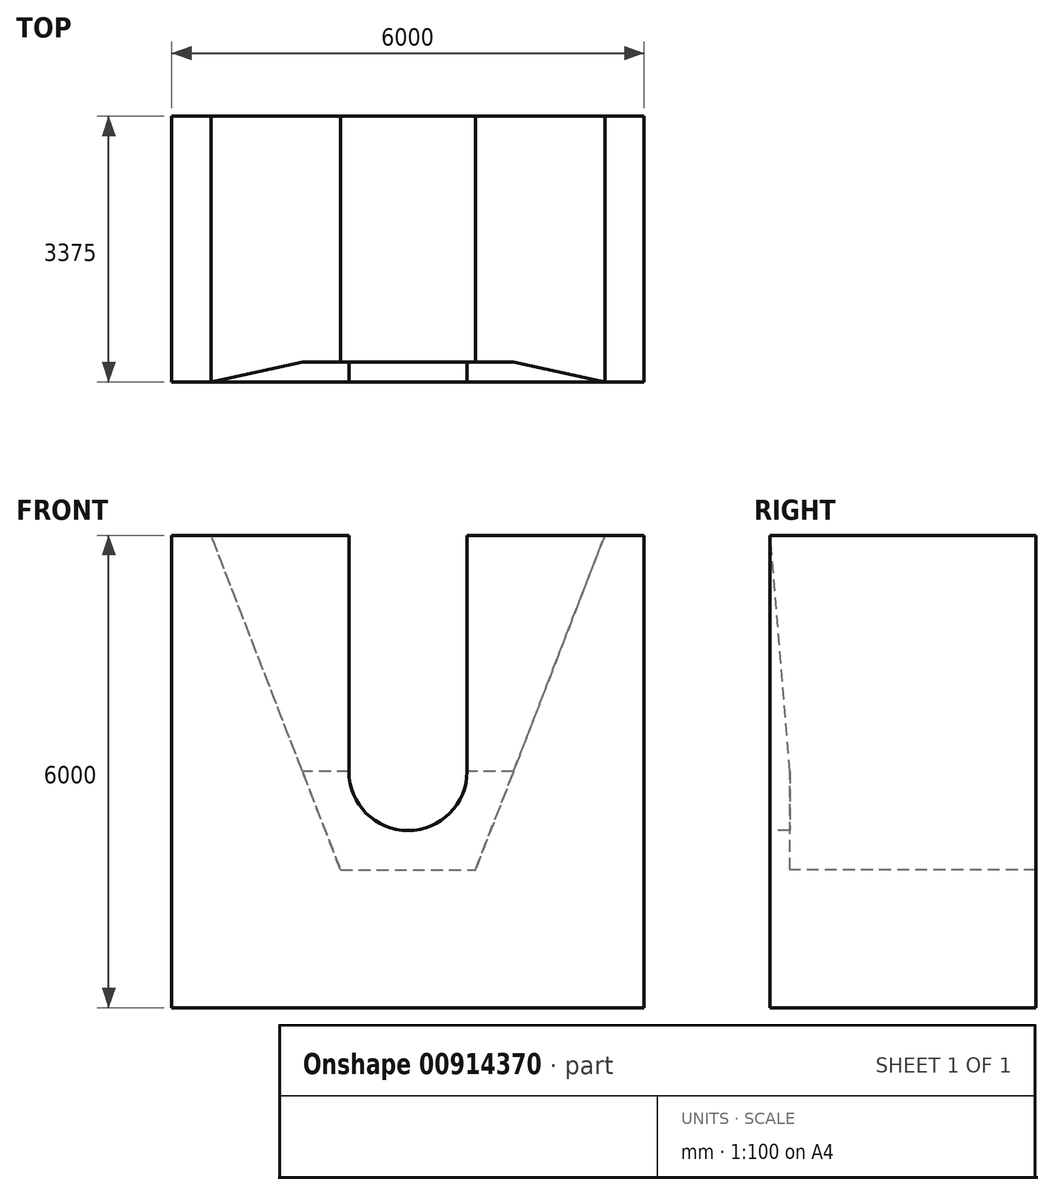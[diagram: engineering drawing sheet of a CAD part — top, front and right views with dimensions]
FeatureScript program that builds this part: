
annotation { "Feature Type Name" : "Feature", "Feature Type Description" : "" }
export const myFeature = defineFeature(function(context is Context, id is Id, definition is map)
    precondition{}
    {
        {
            var Q0;
            Q0=qCreatedBy(makeId("Front.planeOp"),FACE);
            var sketch = newSketch(context, id + "F0", { "sketchPlane" : qUnion([Q0])});
            skLineSegment(sketch, "E0.bottom", {"start": v(-3000, -3000) * mm, "end": v(3000, -3000) * mm, "construction": true});
            skLineSegment(sketch, "E0.top", {"start": v(-3000, 3000) * mm, "end": v(3000, 3000) * mm, "construction": true});
            skLineSegment(sketch, "E0.left", {"start": v(-3000, -3000) * mm, "end": v(-3000, 3000) * mm, "construction": true});
            skLineSegment(sketch, "E0.right", {"start": v(3000, -3000) * mm, "end": v(3000, 3000) * mm, "construction": true});
            skPoint(sketch, "E0.middle", {"position": v(0, 0) * mm});
            skLineSegment(sketch, "E1", {"start": v(3000, 3000) * mm, "end": v(3000, -3000) * mm});
            skLineSegment(sketch, "E2", {"start": v(3000, -3000) * mm, "end": v(-3000, -3000) * mm});
            skLineSegment(sketch, "E3", {"start": v(-3000, 3000) * mm, "end": v(-3000, -3000) * mm});
            skArc(sketch, "E4", {"start": v(-1165.9, -450.75) * mm, "mid": v(0, -1250) * mm, "end": v(1165.9, -450.75) * mm, "construction": true});
            skLineSegment(sketch, "E5", {"start": v(0, 3000) * mm, "end": v(0, -3000) * mm, "construction": true});
            skLineSegment(sketch, "E6", {"start": v(2500, 3000) * mm, "end": v(856.9, -1250) * mm});
            skLineSegment(sketch, "E7", {"start": v(-856.9, -1250) * mm, "end": v(-2500, 3000) * mm});
            skLineSegment(sketch, "E8", {"start": v(2500, 3000) * mm, "end": v(3000, 3000) * mm});
            skLineSegment(sketch, "E9", {"start": v(-2500, 3000) * mm, "end": v(-3000, 3000) * mm});
            skLineSegment(sketch, "E10", {"start": v(856.9, -1250) * mm, "end": v(-856.9, -1250) * mm});
            skSolve(sketch);
        }
        {
            var Q0;
            Q0=makeQuery(id+"F0.imprint","IMPRINT",FACE,{"disambiguationData":[TD([[makeQuery(id+"F0.imprint","IMPRINT",EDGE,{"derivedFrom":sQuery(id+"F0.wireOp",EDGE,"E1")}),-1.0]])]});
            extrude(context, id + "F1", {"entities" : qUnion([Q0]), "oppositeDirection" : true, "depth" : 3375 * mm, "offsetDistance" : 25 * mm});
        }
        {
            var Q0;
            Q0=qCreatedBy(makeId("Front.planeOp"),FACE);
            var sketch = newSketch(context, id + "F2", { "sketchPlane" : qUnion([Q0])});
            skLineSegment(sketch, "E11.bottom", {"start": v(-3000, 3000) * mm, "end": v(3000, 3000) * mm, "construction": true});
            skLineSegment(sketch, "E11.top", {"start": v(-3000, -3000) * mm, "end": v(3000, -3000) * mm});
            skLineSegment(sketch, "E11.left", {"start": v(-3000, 3000) * mm, "end": v(-3000, -3000) * mm});
            skLineSegment(sketch, "E11.right", {"start": v(3000, 3000) * mm, "end": v(3000, -3000) * mm});
            skPoint(sketch, "E11.middle", {"position": v(0, 0) * mm});
            skArc(sketch, "E12", {"start": v(750, 0) * mm, "mid": v(0, -750) * mm, "end": v(-750, 0) * mm});
            skLineSegment(sketch, "E13", {"start": v(750, 0) * mm, "end": v(750, 3000) * mm});
            skLineSegment(sketch, "E14", {"start": v(750, 3000) * mm, "end": v(3000, 3000) * mm});
            skLineSegment(sketch, "E15", {"start": v(-750, 0) * mm, "end": v(-750, 3000) * mm});
            skLineSegment(sketch, "E16", {"start": v(-750, 3000) * mm, "end": v(-3000, 3000) * mm});
            skLineSegment(sketch, "E17", {"start": v(3000, 0) * mm, "end": v(-3000, 0) * mm});
            skSolve(sketch);
        }
        {
            var Q0;
            {var subQ4=sQuery(id+"F2.wireOp",EDGE,"E13");Q0=makeQuery(id+"F2.imprint","IMPRINT",FACE,{"disambiguationData":[TD([[makeQuery(id+"F2.imprint","IMPRINT",EDGE,{"derivedFrom":subQ4}),-1.0]])]});}
            var Q1;
            {var subQ4=sQuery(id+"F2.wireOp",EDGE,"E15");Q1=makeQuery(id+"F2.imprint","IMPRINT",FACE,{"disambiguationData":[TD([[makeQuery(id+"F2.imprint","IMPRINT",EDGE,{"derivedFrom":subQ4}),1.0]])]});}
            extrude(context, id + "F3", {"entities" : qUnion([Q0, Q1]), "oppositeDirection" : true, "depth" : 250 * mm, "offsetDistance" : 25 * mm});
        }
        {
            var Q0;
            Q0=makeQuery(id+"F3.opExtrude","CAP_EDGE",EDGE,{"disambiguationData":[OSD([sQuery(id+"F2.wireOp",EDGE,"E14")])],"isStart":false});
            chamfer(context, id + "F4", {"entities" : qUnion([Q0]), "chamferType" : ChamferType.TWO_OFFSETS, "width1" : 3000 * mm, "oppositeDirection" : false, "width2" : 250 * mm, "tangentPropagation" : true});
        }
        {
            var Q0;
            Q0=makeQuery(id+"F3.opExtrude","CAP_EDGE",EDGE,{"disambiguationData":[OSD([sQuery(id+"F2.wireOp",EDGE,"E16")])],"isStart":false});
            chamfer(context, id + "F5", {"entities" : qUnion([Q0]), "chamferType" : ChamferType.TWO_OFFSETS, "width1" : 3000 * mm, "oppositeDirection" : true, "width2" : 250 * mm, "tangentPropagation" : true});
        }
        {
            var Q0;
            {var subQ1=sQuery(id+"F2.wireOp",EDGE,"E11.top");Q0=makeQuery(id+"F2.imprint","IMPRINT",FACE,{"disambiguationData":[TD([[makeQuery(id+"F2.imprint","IMPRINT",EDGE,{"derivedFrom":subQ1}),1.0]])]});}
            extrude(context, id + "F6", {"entities" : qUnion([Q0]), "operationType" : NewBodyOperationType.ADD, "oppositeDirection" : true, "depth" : 250 * mm, "offsetDistance" : 25 * mm});
        }
    });
